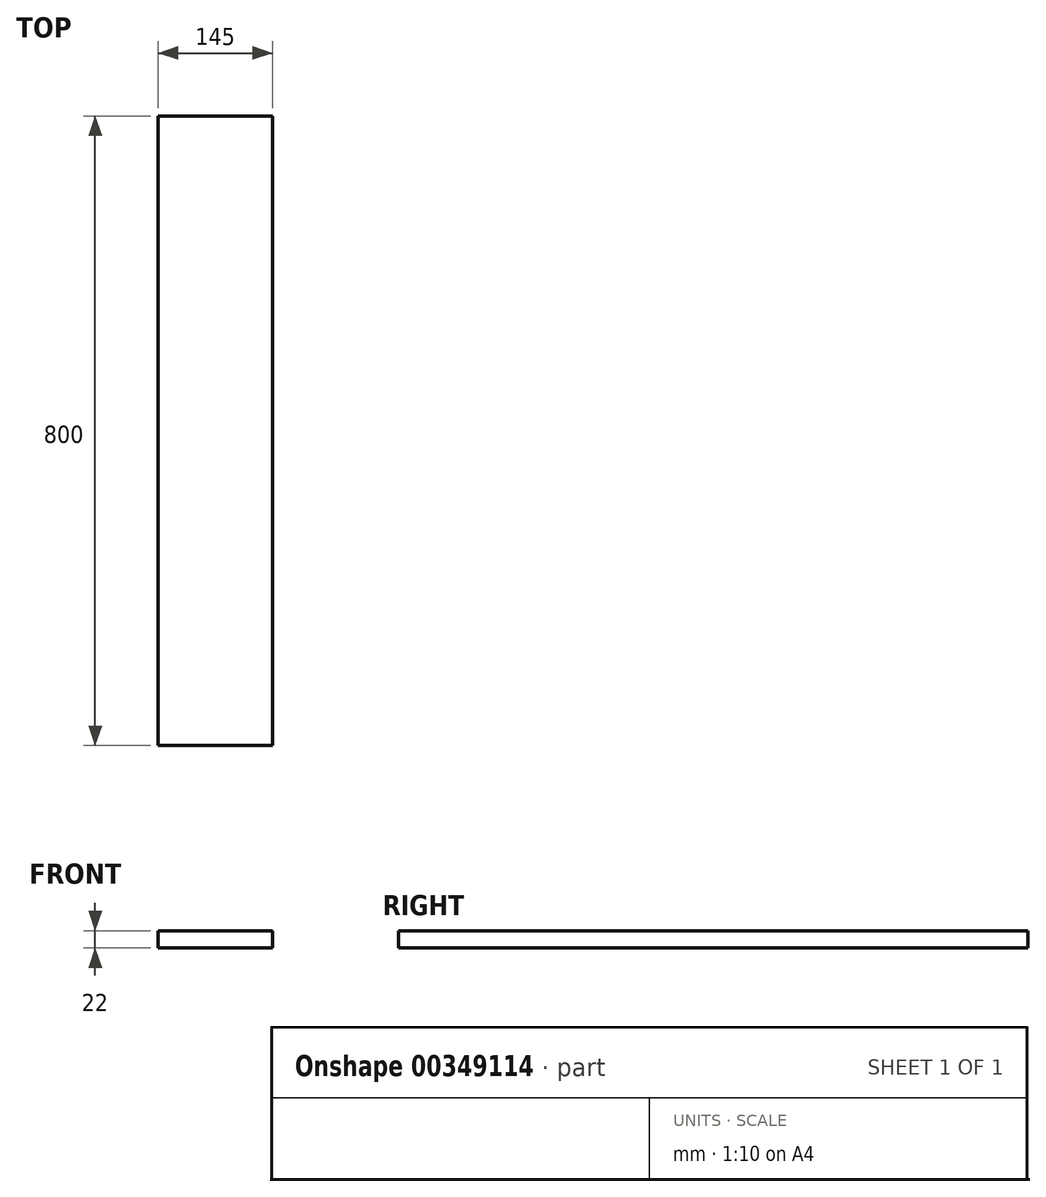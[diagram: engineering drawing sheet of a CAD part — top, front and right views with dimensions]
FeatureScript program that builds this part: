
annotation { "Feature Type Name" : "Feature", "Feature Type Description" : "" }
export const myFeature = defineFeature(function(context is Context, id is Id, definition is map)
    precondition{}
    {
        {
            var Q0;
            Q0=qCreatedBy(makeId("Top.planeOp"),FACE);
            var sketch = newSketch(context, id + "F0", { "sketchPlane" : qUnion([Q0])});
            skLineSegment(sketch, "E0.bottom", {"start": v(-72.5, 400) * mm, "end": v(72.5, 400) * mm});
            skLineSegment(sketch, "E0.top", {"start": v(-72.5, -400) * mm, "end": v(72.5, -400) * mm});
            skLineSegment(sketch, "E0.left", {"start": v(-72.5, 400) * mm, "end": v(-72.5, -400) * mm});
            skLineSegment(sketch, "E0.right", {"start": v(72.5, 400) * mm, "end": v(72.5, -400) * mm});
            skSolve(sketch);
        }
        {
            var Q0;
            Q0 = qSketchRegion(id + "F0", true);
            extrude(context, id + "F1", {"entities" : qUnion([Q0]), "endBound" : BoundingType.SYMMETRIC, "depth" : 22 * mm});
        }
    });
